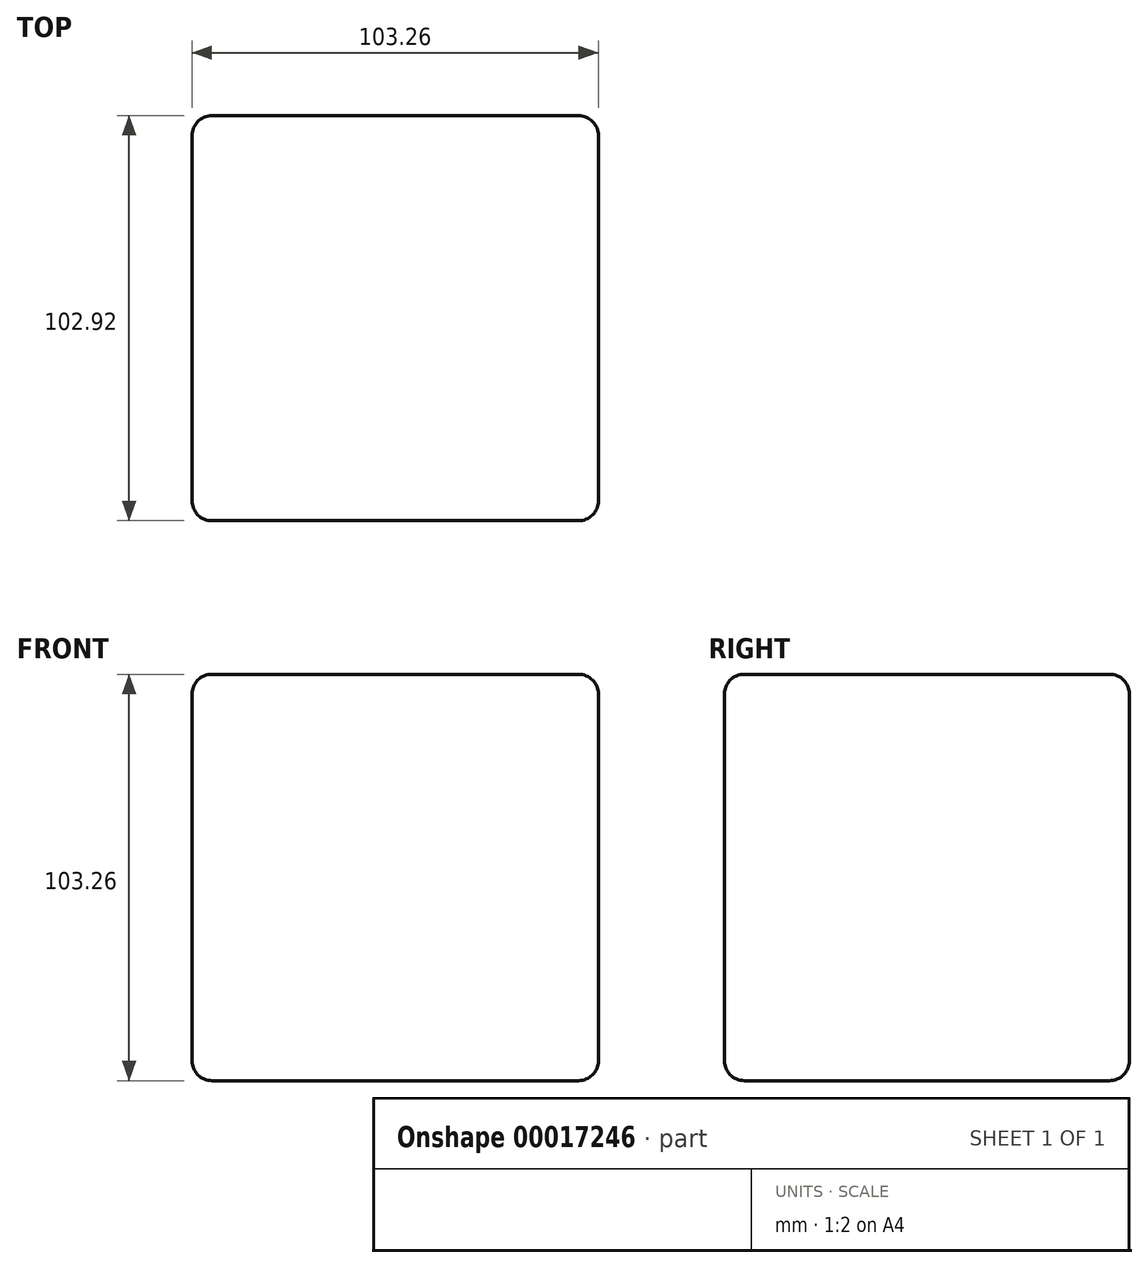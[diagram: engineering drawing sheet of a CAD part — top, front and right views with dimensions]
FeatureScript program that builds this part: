
annotation { "Feature Type Name" : "Feature", "Feature Type Description" : "" }
export const myFeature = defineFeature(function(context is Context, id is Id, definition is map)
    precondition{}
    {
        {
            var Q0;
            Q0=qCreatedBy(makeId("Right.planeOp"),FACE);
            var sketch = newSketch(context, id + "F0", { "sketchPlane" : qUnion([Q0])});
            skLineSegment(sketch, "E0.rect.bottom", {"start": v(68.09, 68.09) * mm, "end": v(-68.09, 68.09) * mm});
            skLineSegment(sketch, "E0.rect.top", {"start": v(68.09, -68.09) * mm, "end": v(-68.09, -68.09) * mm});
            skLineSegment(sketch, "E0.rect.left", {"start": v(68.09, 68.09) * mm, "end": v(68.09, -68.09) * mm});
            skLineSegment(sketch, "E0.rect.right", {"start": v(-68.09, 68.09) * mm, "end": v(-68.09, -68.09) * mm});
            skPoint(sketch, "E0.rect.middle", {"position": v(0, 0) * mm});
            skSolve(sketch);
        }
        {
            var Q0;
            Q0=makeQuery(id+"F0.imprint","IMPRINT",FACE,{"disambiguationData":[TD([[makeQuery(id+"F0.imprint","IMPRINT",EDGE,{"derivedFrom":sQuery(id+"F0.wireOp",EDGE,"E0.rect.bottom")}),1.0]])]});
            extrude(context, id + "F1", {"entities" : qUnion([Q0]), "endBound" : BoundingType.SYMMETRIC, "depth" : 69.83 * mm});
        }
        {
            var Q0;
            Q0=makeQuery(id+"F1.opExtrude","SWEPT_BODY",BODY,{"disambiguationData":[OSD([sQuery(id+"F0.wireOp",EDGE,"E0.rect.bottom"),sQuery(id+"F0.wireOp",EDGE,"E0.rect.top"),sQuery(id+"F0.wireOp",EDGE,"E0.rect.left"),sQuery(id+"F0.wireOp",EDGE,"E0.rect.right")])]});
            deleteBodies(context, id + "F2", {"entities" : qUnion([Q0])});
        }
        {
            var Q0;
            Q0=qCreatedBy(makeId("Front.planeOp"),FACE);
            var sketch = newSketch(context, id + "F3", { "sketchPlane" : qUnion([Q0])});
            skLineSegment(sketch, "E1.rect.bottom", {"start": v(51.63, -51.63) * mm, "end": v(-51.63, -51.63) * mm});
            skLineSegment(sketch, "E1.rect.top", {"start": v(51.63, 51.63) * mm, "end": v(-51.63, 51.63) * mm});
            skLineSegment(sketch, "E1.rect.left", {"start": v(51.63, -51.63) * mm, "end": v(51.63, 51.63) * mm});
            skLineSegment(sketch, "E1.rect.right", {"start": v(-51.63, -51.63) * mm, "end": v(-51.63, 51.63) * mm});
            skPoint(sketch, "E1.rect.middle", {"position": v(0, 0) * mm});
            skSolve(sketch);
        }
        {
            var Q0;
            Q0=makeQuery(id+"F3.imprint","IMPRINT",FACE,{"disambiguationData":[TD([[makeQuery(id+"F3.imprint","IMPRINT",EDGE,{"derivedFrom":sQuery(id+"F3.wireOp",EDGE,"E1.rect.bottom")}),-1.0]])]});
            extrude(context, id + "F4", {"entities" : qUnion([Q0]), "depth" : 102.92 * mm});
        }
        {
            var Q0;
            Q0=makeQuery(id+"F4.opExtrude","CAP_EDGE",EDGE,{"disambiguationData":[OSD([sQuery(id+"F3.wireOp",EDGE,"E1.rect.top")])],"isStart":false});
            fillet(context, id + "F5", {"entities" : qUnion([Q0]), "radius" : 5.08 * mm, "tangentPropagation" : true, "allowEdgeOverflow" : false});
        }
        {
            var Q0;
            Q0=makeQuery(id+"F4.opExtrude","SWEPT_EDGE",EDGE,{"disambiguationData":[OSD([sQuery(id+"F3.wireOp",EDGE,"E1.rect.top"),sQuery(id+"F3.wireOp",EDGE,"E1.rect.left")])]});
            fillet(context, id + "F6", {"entities" : qUnion([Q0]), "radius" : 5.08 * mm, "tangentPropagation" : true, "allowEdgeOverflow" : false});
        }
        {
            var Q0;
            Q0=makeQuery(id+"F4.opExtrude","SWEPT_EDGE",EDGE,{"disambiguationData":[OSD([sQuery(id+"F3.wireOp",EDGE,"E1.rect.top"),sQuery(id+"F3.wireOp",EDGE,"E1.rect.right")])]});
            var Q1;
            Q1=makeQuery(id+"F4.opExtrude","CAP_EDGE",EDGE,{"disambiguationData":[OSD([sQuery(id+"F3.wireOp",EDGE,"E1.rect.right")])],"isStart":false});
            var Q2;
            Q2=makeQuery(id+"F4.opExtrude","CAP_EDGE",EDGE,{"disambiguationData":[OSD([sQuery(id+"F3.wireOp",EDGE,"E1.rect.bottom")])],"isStart":false});
            var Q3;
            Q3=makeQuery(id+"F4.opExtrude","SWEPT_EDGE",EDGE,{"disambiguationData":[OSD([sQuery(id+"F3.wireOp",EDGE,"E1.rect.bottom"),sQuery(id+"F3.wireOp",EDGE,"E1.rect.right")])]});
            var Q4;
            Q4=makeQuery(id+"F4.opExtrude","SWEPT_EDGE",EDGE,{"disambiguationData":[OSD([sQuery(id+"F3.wireOp",EDGE,"E1.rect.bottom"),sQuery(id+"F3.wireOp",EDGE,"E1.rect.left")])]});
            var Q5;
            Q5=makeQuery(id+"F4.opExtrude","CAP_EDGE",EDGE,{"disambiguationData":[OSD([sQuery(id+"F3.wireOp",EDGE,"E1.rect.right")])],"isStart":true});
            var Q6;
            Q6=makeQuery(id+"F4.opExtrude","CAP_EDGE",EDGE,{"disambiguationData":[OSD([sQuery(id+"F3.wireOp",EDGE,"E1.rect.bottom")])],"isStart":true});
            var Q7;
            Q7=makeQuery(id+"F4.opExtrude","CAP_EDGE",EDGE,{"disambiguationData":[OSD([sQuery(id+"F3.wireOp",EDGE,"E1.rect.top")])],"isStart":true});
            var Q8;
            Q8=makeQuery(id+"F4.opExtrude","CAP_EDGE",EDGE,{"disambiguationData":[OSD([sQuery(id+"F3.wireOp",EDGE,"E1.rect.left")])],"isStart":true});
            fillet(context, id + "F7", {"entities" : qUnion([Q0, Q1, Q2, Q3, Q4, Q5, Q6, Q7, Q8]), "radius" : 5.08 * mm, "tangentPropagation" : true, "allowEdgeOverflow" : false});
        }
    });
